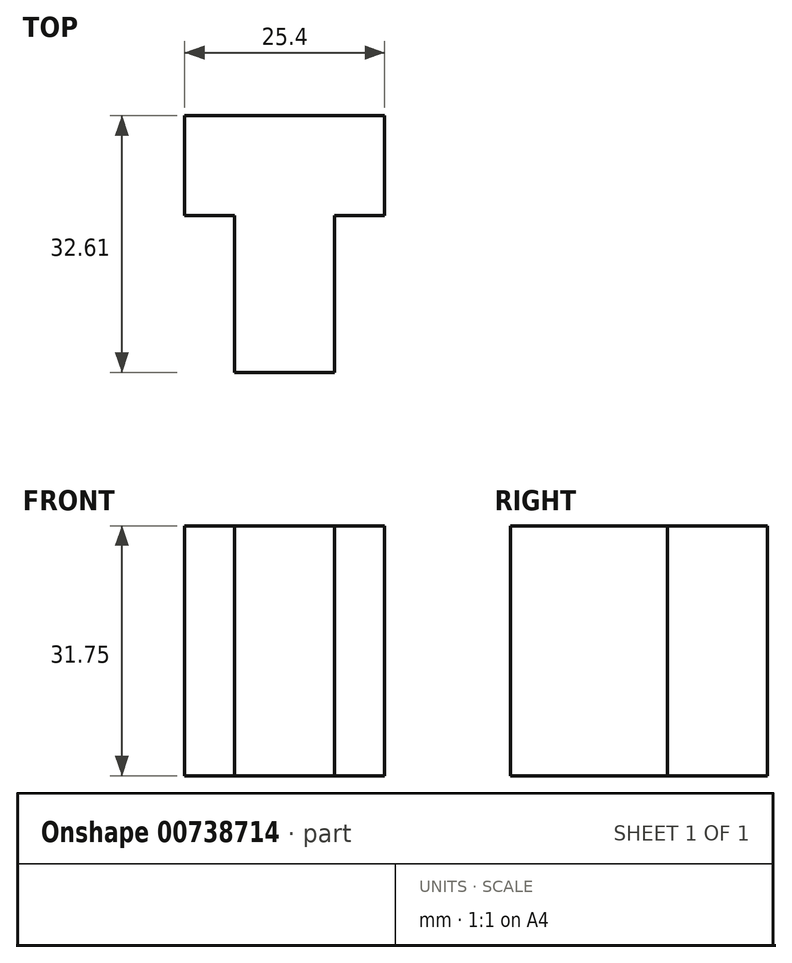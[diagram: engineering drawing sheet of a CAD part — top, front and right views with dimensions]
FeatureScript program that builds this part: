
annotation { "Feature Type Name" : "Feature", "Feature Type Description" : "" }
export const myFeature = defineFeature(function(context is Context, id is Id, definition is map)
    precondition{}
    {
        {
            var Q0;
            Q0=qCreatedBy(makeId("Top.planeOp"),FACE);
            var sketch = newSketch(context, id + "F0", { "sketchPlane" : qUnion([Q0])});
            skLineSegment(sketch, "E0", {"start": v(0, 32.61) * mm, "end": v(25.4, 32.61) * mm});
            skLineSegment(sketch, "E1", {"start": v(25.4, 32.61) * mm, "end": v(25.4, 19.91) * mm});
            skLineSegment(sketch, "E2", {"start": v(25.4, 19.91) * mm, "end": v(19.05, 19.91) * mm});
            skLineSegment(sketch, "E3", {"start": v(19.05, 19.91) * mm, "end": v(19.05, 0) * mm});
            skLineSegment(sketch, "E4", {"start": v(19.05, 0) * mm, "end": v(6.35, 0) * mm});
            skLineSegment(sketch, "E5", {"start": v(6.35, 0) * mm, "end": v(6.35, 19.91) * mm});
            skLineSegment(sketch, "E6", {"start": v(6.35, 19.91) * mm, "end": v(0, 19.91) * mm});
            skLineSegment(sketch, "E7", {"start": v(0, 19.91) * mm, "end": v(0, 32.61) * mm});
            skSolve(sketch);
        }
        {
            var Q0;
            Q0 = qSketchRegion(id + "F0", true);
            extrude(context, id + "F1", {"entities" : qUnion([Q0]), "depth" : 31.75 * mm, "offsetDistance" : 25.4 * mm});
        }
    });
